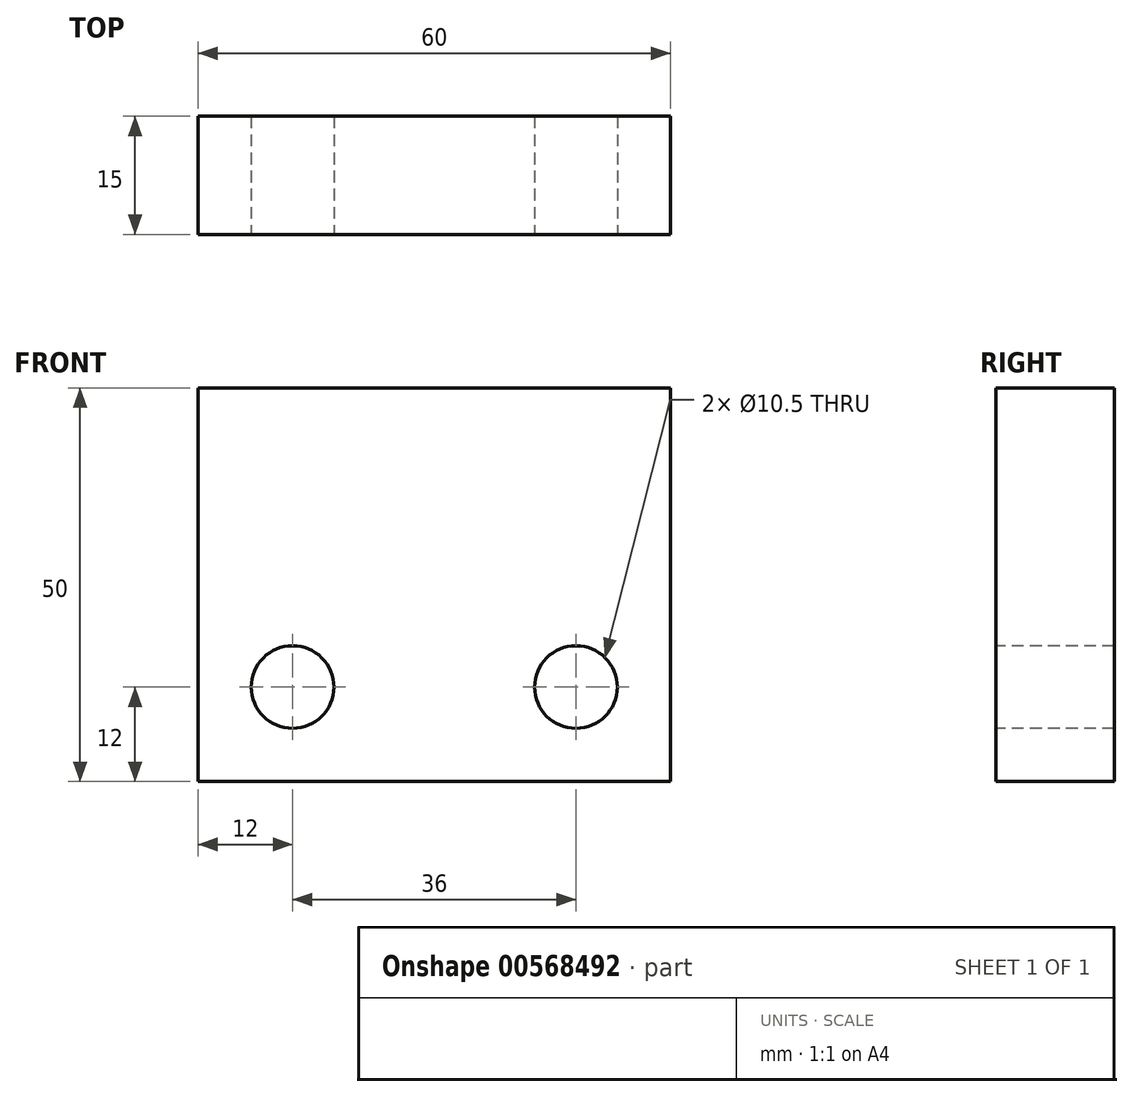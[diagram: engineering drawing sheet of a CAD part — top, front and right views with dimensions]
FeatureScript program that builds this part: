
annotation { "Feature Type Name" : "Feature", "Feature Type Description" : "" }
export const myFeature = defineFeature(function(context is Context, id is Id, definition is map)
    precondition{}
    {
        {
            var Q0;
            Q0=qCreatedBy(makeId("Front.planeOp"),FACE);
            var sketch = newSketch(context, id + "F0", { "sketchPlane" : qUnion([Q0])});
            skLineSegment(sketch, "E0", {"start": v(0, 0) * mm, "end": v(0, 148.23) * mm, "construction": true});
            skLineSegment(sketch, "E1", {"start": v(0, 0) * mm, "end": v(116.92, 0) * mm, "construction": true});
            skLineSegment(sketch, "E2.bottom", {"start": v(-30, -25) * mm, "end": v(30, -25) * mm});
            skLineSegment(sketch, "E2.top", {"start": v(-30, 25) * mm, "end": v(30, 25) * mm});
            skLineSegment(sketch, "E2.left", {"start": v(-30, -25) * mm, "end": v(-30, 25) * mm});
            skLineSegment(sketch, "E2.right", {"start": v(30, -25) * mm, "end": v(30, 25) * mm});
            skSolve(sketch);
        }
        {
            var Q0;
            Q0=makeQuery(id+"F0.imprint","IMPRINT",FACE,{"disambiguationData":[TD([[makeQuery(id+"F0.imprint","IMPRINT",EDGE,{"derivedFrom":sQuery(id+"F0.wireOp",EDGE,"E2.bottom")}),1.0]])]});
            extrude(context, id + "F1", {"entities" : qUnion([Q0]), "endBound" : BoundingType.SYMMETRIC, "depth" : 15 * mm, "offsetDistance" : 25 * mm});
        }
        {
            var Q0;
            Q0=makeQuery(id+"F1.opExtrude","CAP_FACE",FACE,{"disambiguationData":[OSD([sQuery(id+"F0.wireOp",EDGE,"E2.bottom"),sQuery(id+"F0.wireOp",EDGE,"E2.top"),sQuery(id+"F0.wireOp",EDGE,"E2.left"),sQuery(id+"F0.wireOp",EDGE,"E2.right")])],"isStart":false});
            var sketch = newSketch(context, id + "F2", { "sketchPlane" : qUnion([Q0])});
            skPoint(sketch, "E3", {"position": v(18, -13) * mm});
            skPoint(sketch, "E4", {"position": v(-18, -13) * mm});
            skSolve(sketch);
        }
        {
            var Q0;
            Q0=sQuery(id+"F2.wireOp",VERTEX,"E3");
            var Q1;
            Q1=sQuery(id+"F2.wireOp",VERTEX,"E4");
            var Q2;
            Q2=makeQuery(id+"F1.opExtrude","SWEPT_BODY",BODY,{"disambiguationData":[OSD([sQuery(id+"F0.wireOp",EDGE,"E2.bottom"),sQuery(id+"F0.wireOp",EDGE,"E2.top"),sQuery(id+"F0.wireOp",EDGE,"E2.left"),sQuery(id+"F0.wireOp",EDGE,"E2.right")])]});
            hole(context, id + "F3", {"style" : HoleStyle.SIMPLE, "endStyle" : HoleEndStyle.THROUGH, "holeDiameter" : 10.5 * mm, "majorDiameter" : 5 * mm, "isTappedThrough" : true, "tappedDepth" : 12 * mm, "tapClearance" : 3, "locations" : qUnion([Q0, Q1]), "scope" : qUnion([Q2])});
        }
    });
